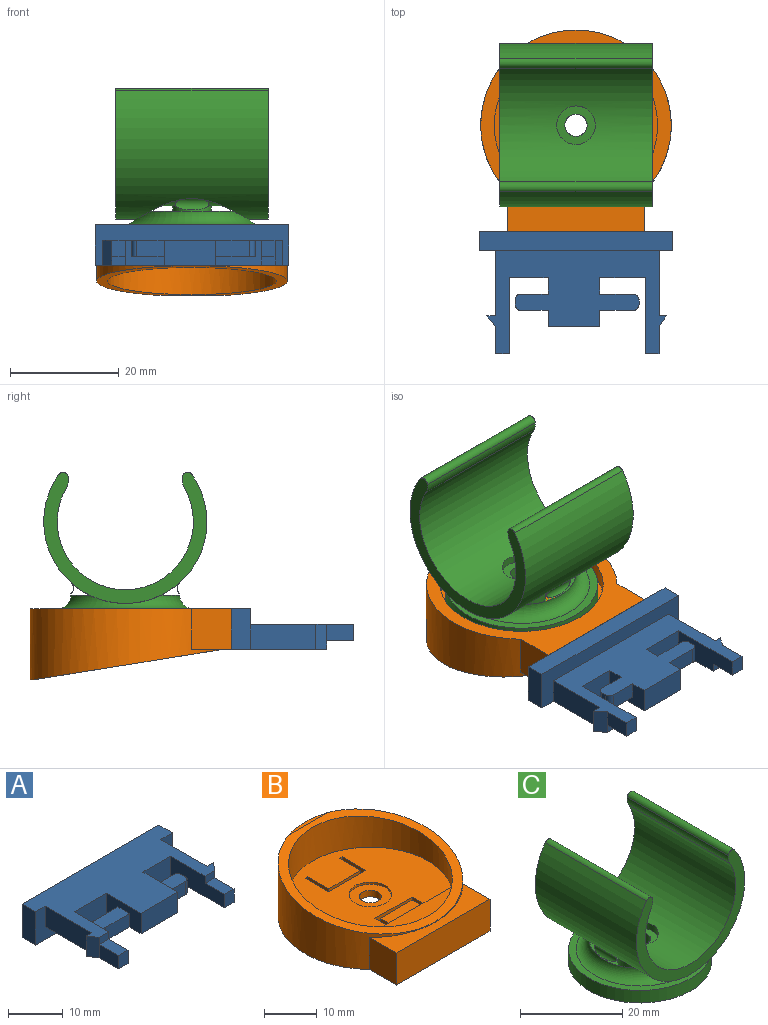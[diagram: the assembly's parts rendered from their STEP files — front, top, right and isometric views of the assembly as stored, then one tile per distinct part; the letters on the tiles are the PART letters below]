
ASSEMBLY  parts=3 mates=2
PART A: 40 faces, bbox 35.5x22.5x7.5 mm
  f0: plane 32.98x19mm, normal (0,0,-1), area 347.2mm2, adj f1,f2,f4,f5,f6,f7,f10,f13
  f1: plane 4.6x1.65mm, normal (0,1,0), area 7.6mm2, adj f0,f3,f14,f38
  f2: plane 9x4.6mm, normal (1,0,0), area 32.4mm2, adj f0,f3,f6,f16,f26,f27,f28
  f3: plane 35.5x17.5mm, normal (0,0,1), area 407.7mm2, adj f1,f2,f6,f7,f8,f9,f10,f11
  f4: plane 5x3mm, normal (1,0,0), area 15mm2, adj f0,f20,f24,f38
  f5: plane 5x3mm, normal (-1,0,0), area 15mm2, adj f0,f18,f25,f39
  f6: plane 7.12x4.6mm, normal (0,-1,0), area 32.8mm2, adj f0,f2,f3,f19
  f7: plane 8.38x4.6mm, normal (0,-1,0), area 38.5mm2, adj f0,f3,f15,f17
  f8: plane 35.5x7.5mm, normal (0,1,0), area 266.2mm2, adj f3,f9,f11,f12
  f9: plane 7.5x3.5mm, normal (-1,0,0), area 26.2mm2, adj f3,f8,f10,f12
  f10: plane 35.5x7.5mm, normal (0,-1,0), area 128.2mm2, adj f0,f3,f9,f11,f12,f13,f14
  f11: plane 7.5x3.5mm, normal (1,0,0), area 26.2mm2, adj f3,f8,f10,f12
  f12: plane 35.5x3.5mm, normal (0,0,-1), area 124.2mm2, adj f8,f9,f10,f11
  f13: plane 12x4.6mm, normal (-1,0,0), area 55.2mm2, adj f0,f3,f10,f22
  f14: plane 12x4.6mm, normal (1,0,0), area 55.2mm2, adj f0,f1,f3,f10
  f15: plane 9x4.6mm, normal (-1,0,0), area 32.4mm2, adj f0,f3,f7,f16,f30,f31,f32
  f16: plane 9.5x4.6mm, normal (0,-1,0), area 43.7mm2, adj f0,f2,f3,f15
  f17: plane 14x4.6mm, normal (1,0,0), area 56.4mm2, adj f0,f3,f7,f18,f21,f25
  f18: plane 3x2.5mm, normal (0,-1,0), area 7.5mm2, adj f0,f5,f17,f25
  f19: plane 14x4.6mm, normal (-1,0,0), area 56.4mm2, adj f0,f3,f6,f20,f23,f24
  f20: plane 3x2.5mm, normal (0,-1,0), area 7.5mm2, adj f0,f4,f19,f24
  f21: plane 2.5x1.6mm, normal (0,-1,0), area 4mm2, adj f3,f17,f25,f39
  f22: plane 4.6x1.33mm, normal (0,1,0), area 6.1mm2, adj f0,f3,f13,f39
  f23: plane 2.5x1.6mm, normal (0,-1,0), area 4mm2, adj f3,f19,f24,f38
  f24: plane 5x2.5mm, normal (0,0,1), area 12.5mm2, adj f4,f19,f20,f23
  f25: plane 5x2.5mm, normal (0,0,1), area 12.5mm2, adj f5,f17,f18,f21
  f26: plane 5.03x3mm, normal (0,-1,0), area 15.1mm2, adj f0,f2,f28,f37
  f27: plane 5.03x3mm, normal (0,1,0), area 15.1mm2, adj f0,f2,f28,f36
  f28: plane 6x3mm, normal (0,0,1), area 17.6mm2, adj f2,f26,f27,f29,f36,f37
  f29: plane 3x1.07mm, normal (1,0,0), area 3.2mm2, adj f0,f28,f36,f37
  f30: plane 6.14x3mm, normal (0,1,0), area 18.4mm2, adj f0,f15,f32,f35
  f31: plane 6.14x3mm, normal (0,-1,0), area 18.4mm2, adj f0,f15,f32,f34
  f32: plane 7.2x3mm, normal (0,0,1), area 21.1mm2, adj f15,f30,f31,f33,f34,f35
  f33: plane 3x0.88mm, normal (-1,0,0), area 2.6mm2, adj f0,f32,f34,f35
  f34: cylinder r=1.06mm len=3mm, axis (0,0,-1), area 5mm2, adj f0,f31,f32,f33
  f35: cylinder r=1.06mm len=3mm, axis (0,0,1), area 5mm2, adj f0,f30,f32,f33
  f36: cylinder r=0.97mm len=3mm, axis (0,0,-1), area 4.6mm2, adj f0,f27,f28,f29
  f37: cylinder r=0.97mm len=3mm, axis (0,0,1), area 4.6mm2, adj f0,f26,f28,f29
  f38: plane 4.6x2mm, normal (0.77,-0.64,0), area 11.9mm2, adj f0,f1,f3,f4,f23
  f39: plane 4.6x2mm, normal (-0.83,-0.55,0), area 11.1mm2, adj f0,f3,f5,f21,f22
PART B: 40 faces, bbox 35.8x37.8x13.8 mm
  f0: cylinder r=2.05mm len=4.1mm, axis (0,0,1), area 19.3mm2, adj f3,f39
  f1: plane 31x27mm, normal (0,0,1), area 578.6mm2, adj f8,f10,f11,f17,f18,f19,f20,f21
  f2: plane 8.53x4.63mm, normal (0,0,1), area 39.5mm2, adj f13,f14,f15,f27
  f3: plane 30x30mm, normal (0,0,-1), area 654.3mm2, adj f0,f9,f10,f11,f12,f13,f14,f15
  f4: cylinder r=17.5mm len=35mm, axis (0,0,-1), area 919.6mm2, adj f5,f6,f7,f30,f31,f32
  f5: plane 10.53x0.81mm, normal (0,0,1), area 5.7mm2, adj f4,f7
  f6: plane 37x35mm, normal (0,0,-1), area 346mm2, adj f4,f9,f30,f31,f33
  f7: plane 35.85x35.04mm, normal (0,-0.16,0.99), area 204.2mm2, adj f4,f5,f8
  f8: cylinder r=15.5mm len=31mm, axis (0,0,1), area 463mm2, adj f1,f7,f26,f27
  f9: cylinder r=15mm len=30mm, axis (0,0,-1), area 282.7mm2, adj f3,f6
  f10: plane 9.92x2mm, normal (0,-1,0), area 19.8mm2, adj f1,f3,f11,f17
  f11: plane 6.33x2mm, normal (1,0,0), area 12.7mm2, adj f1,f3,f10,f12,f28
  f12: plane 2x0.7mm, normal (0,1,0), area 1.4mm2, adj f3,f11,f13,f28
  f13: plane 5.64x2mm, normal (-1,0,0), area 11.3mm2, adj f2,f3,f12,f14,f28
  f14: plane 8.53x2mm, normal (0,1,0), area 17.1mm2, adj f2,f3,f13,f15
  f15: plane 5.64x2mm, normal (1,0,0), area 11.3mm2, adj f2,f3,f14,f16,f29
  f16: plane 2x0.7mm, normal (0,1,0), area 1.4mm2, adj f3,f15,f17,f29
  f17: plane 6.33x2mm, normal (-1,0,0), area 12.7mm2, adj f1,f3,f10,f16,f29
  f18: plane 6.33x2mm, normal (-1,0,0), area 12.7mm2, adj f1,f3,f19,f25
  f19: plane 2x0.7mm, normal (0,-1,0), area 1.4mm2, adj f1,f3,f18,f20
  f20: plane 5.64x2mm, normal (1,0,0), area 11.3mm2, adj f1,f3,f19,f21
  f21: plane 8.53x2mm, normal (0,-1,0), area 17.1mm2, adj f1,f3,f20,f22
  f22: plane 5.64x2mm, normal (-1,0,0), area 11.3mm2, adj f1,f3,f21,f23
  f23: plane 2x0.7mm, normal (0,-1,0), area 1.4mm2, adj f1,f3,f22,f24
  f24: plane 6.33x2mm, normal (1,0,0), area 12.7mm2, adj f1,f3,f23,f25
  f25: plane 9.92x2mm, normal (0,1,0), area 19.8mm2, adj f1,f3,f18,f24
  f26: plane 20.78x4mm, normal (0,0,1), area 57mm2, adj f8,f27
  f27: plane 20.78x2.4mm, normal (0,1,0), area 49.9mm2, adj f1,f2,f8,f26,f28,f29
  f28: plane 1.01x0.7mm, normal (0,0,-1), area 0.7mm2, adj f11,f12,f13,f27
  f29: plane 1.01x0.7mm, normal (0,0,-1), area 0.7mm2, adj f15,f16,f17,f27
  f30: plane 7.4x7.25mm, normal (1,0,0), area 53.7mm2, adj f4,f6,f32,f33
  f31: plane 7.4x7.25mm, normal (-1,0,0), area 53.7mm2, adj f4,f6,f32,f33
  f32: plane 25x7.25mm, normal (0,0,1), area 90.8mm2, adj f4,f30,f31,f33
  f33: plane 25x7.4mm, normal (0,-1,0), area 185mm2, adj f6,f30,f31,f32
  f34: plane 0.77x0.77mm, normal (0,0,-1), area 0.5mm2, adj f37
  f35: plane 0.77x0.77mm, normal (0,0,-1), area 0.5mm2, adj f36
  f36: torus R=0.38mm, axis (0,0,1), area 5.7mm2, adj f3,f35
  f37: torus R=0.38mm, axis (0,0,1), area 5.7mm2, adj f3,f34
  f38: cylinder r=4.05mm len=8.1mm, axis (0,0,1), area 12.7mm2, adj f1,f39
  f39: plane 8.1x8.1mm, normal (0,0,1), area 38.3mm2, adj f0,f38
PART C: 21 faces, bbox 30.9x30.9x28.1 mm
  f0: cylinder r=2.05mm len=4.1mm, axis (0,0,-1), area 43.8mm2, adj f18,f20
  f1: cylinder r=12.5mm len=28mm, axis (0,1,0), area 1420.4mm2, adj f9,f10,f13,f14,f17
  f2: cylinder r=10mm len=15.18mm, axis (0,0,-1), area 14.4mm2, adj f4,f8,f12
  f3: cylinder r=10mm len=15.18mm, axis (0,0,-1), area 14.4mm2, adj f4,f8,f11
  f4: torus R=12.49mm, axis (0,0,1), area 238.9mm2, adj f2,f3,f6,f8
  f5: cylinder r=14mm len=28mm, axis (0,0,-1), area 263.9mm2, adj f6,f7
  f6: plane 28x28mm, normal (0,0,1), area 125.9mm2, adj f4,f5
  f7: plane 28x28mm, normal (0,0,-1), area 557mm2, adj f5,f19
  f8: cylinder r=15mm len=30mm, axis (0,1,0), area 1493.3mm2, adj f2,f3,f4,f9,f10,f11,f12,f15
  f9: plane 30x24.07mm, normal (0,-1,0), area 153.2mm2, adj f1,f8,f13,f14,f15,f16
  f10: plane 30x24.07mm, normal (0,1,0), area 153.2mm2, adj f1,f8,f13,f14,f15,f16
  f11: cylinder r=1.3mm len=6.23mm, axis (0,1,0), area 11.3mm2, adj f3,f8
  f12: cylinder r=1.3mm len=6.23mm, axis (0,1,0), area 11.3mm2, adj f2,f8
  f13: cylinder r=3.44mm len=28mm, axis (0,1,0), area 58.1mm2, adj f1,f9,f10,f15
  f14: cylinder r=3.44mm len=28mm, axis (0,-1,0), area 58.1mm2, adj f1,f9,f10,f16
  f15: cylinder r=1mm len=28mm, axis (0,1,0), area 68.3mm2, adj f8,f9,f10,f13
  f16: cylinder r=1mm len=28mm, axis (0,-1,0), area 68.3mm2, adj f8,f9,f10,f14
  f17: cylinder r=3.55mm len=7.1mm, axis (0,0,1), area 28mm2, adj f1,f18
  f18: plane 7.1x7.1mm, normal (0,0,1), area 26.4mm2, adj f0,f17
  f19: cylinder r=4.33mm len=8.65mm, axis (0,0,-1), area 57.1mm2, adj f7,f20
  f20: plane 8.65x8.65mm, normal (0,0,-1), area 45.6mm2, adj f0,f19
PLACE A rot(axis=(0,-1,0),180deg) t=(-1.65,20.12,6.08)mm
PLACE B rot(axis=(0,-1,0),180deg) t=(-1.65,22.12,6.03)mm
PLACE C rot(axis=(0,0,-1),90deg) t=(-1.65,22.12,3.03)mm
MATE revolute B.f0 <-> C.f5  axis (0,0,1) through (-1.65,22.12,3.03)mm
MATE fastened B.f33 <-> A.f8  axis (0,-1,0) through (-1.65,2.62,2.33)mm
